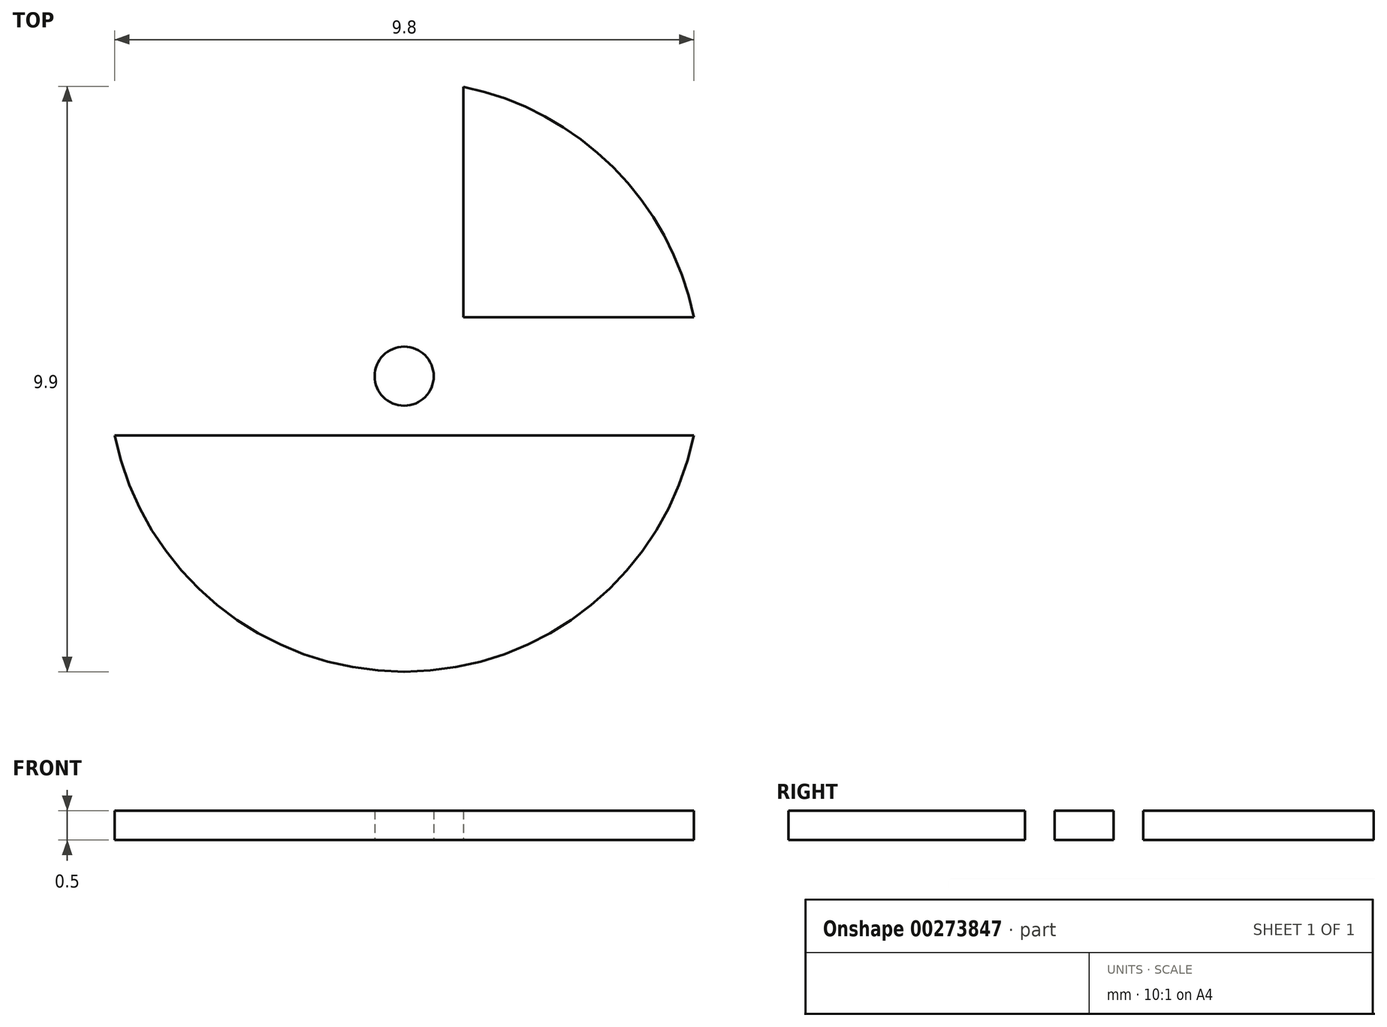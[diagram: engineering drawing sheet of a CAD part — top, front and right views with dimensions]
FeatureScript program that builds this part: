
annotation { "Feature Type Name" : "Feature", "Feature Type Description" : "" }
export const myFeature = defineFeature(function(context is Context, id is Id, definition is map)
    precondition{}
    {
        {
            var Q0;
            Q0=qCreatedBy(makeId("Top.planeOp"),FACE);
            var sketch = newSketch(context, id + "F0", { "sketchPlane" : qUnion([Q0])});
            skCircle(sketch, "E0", {"center": v(0, 0) * mm, "radius": 5 * mm});
            skLineSegment(sketch, "E1.bottom", {"start": v(-1, 12.5) * mm, "end": v(1, 12.5) * mm});
            skLineSegment(sketch, "E1.top", {"start": v(-1, -12.5) * mm, "end": v(1, -12.5) * mm});
            skLineSegment(sketch, "E1.left", {"start": v(-1, 12.5) * mm, "end": v(-1, -12.5) * mm});
            skLineSegment(sketch, "E1.right", {"start": v(1, 12.5) * mm, "end": v(1, -12.5) * mm});
            skLineSegment(sketch, "E2.bottom", {"start": v(-12.5, 1) * mm, "end": v(12.5, 1) * mm});
            skLineSegment(sketch, "E2.top", {"start": v(-12.5, -1) * mm, "end": v(12.5, -1) * mm});
            skLineSegment(sketch, "E2.left", {"start": v(-12.5, 1) * mm, "end": v(-12.5, -1) * mm});
            skLineSegment(sketch, "E2.right", {"start": v(12.5, 1) * mm, "end": v(12.5, -1) * mm});
            skCircle(sketch, "E3", {"center": v(0, 0) * mm, "radius": 1 * mm});
            skCircle(sketch, "E4", {"center": v(0, 0) * mm, "radius": 0.5 * mm});
            skSolve(sketch);
        }
        {
            var Q0;
            Q0=makeQuery(id+"F0.imprint","IMPRINT",FACE,{"disambiguationData":[TD([[makeQuery(id+"F0.imprint","IMPRINT",EDGE,{"derivedFrom":sQuery(id+"F0.wireOp",EDGE,"E4")}),1.0]])]});
            var Q1;
            {var subQ0=sQuery(id+"F0.wireOp",EDGE,"E1.left");var subQ1=sQuery(id+"F0.wireOp",EDGE,"E0");var subQ2=makeQuery(id+"F0.imprint","INTERSECT",VERTEX,{"disambiguationData":[OD(0.0)],"derivedFrom":[subQ1,subQ0]});Q1=makeQuery(id+"F0.imprint","IMPRINT",FACE,{"disambiguationData":[TD([[makeQuery(id+"F0.imprint","IMPRINT",EDGE,{"disambiguationData":[TD([[subQ2,-1.0]])],"derivedFrom":subQ1}),1.0]])]});}
            var Q2;
            {var subQ0=sQuery(id+"F0.wireOp",EDGE,"E1.right");var subQ1=sQuery(id+"F0.wireOp",EDGE,"E0");var subQ2=makeQuery(id+"F0.imprint","INTERSECT",VERTEX,{"disambiguationData":[OD(0.0)],"derivedFrom":[subQ1,subQ0]});Q2=makeQuery(id+"F0.imprint","IMPRINT",FACE,{"disambiguationData":[TD([[makeQuery(id+"F0.imprint","IMPRINT",EDGE,{"disambiguationData":[TD([[subQ2,1.0]])],"derivedFrom":subQ1}),1.0]])]});}
            var Q3;
            {var subQ0=sQuery(id+"F0.wireOp",EDGE,"E1.right");var subQ1=sQuery(id+"F0.wireOp",EDGE,"E0");var subQ2=makeQuery(id+"F0.imprint","INTERSECT",VERTEX,{"disambiguationData":[OD(1.0)],"derivedFrom":[subQ1,subQ0]});Q3=makeQuery(id+"F0.imprint","IMPRINT",FACE,{"disambiguationData":[TD([[makeQuery(id+"F0.imprint","IMPRINT",EDGE,{"disambiguationData":[TD([[subQ2,-1.0]])],"derivedFrom":subQ1}),1.0]])]});}
            var Q4;
            {var subQ0=sQuery(id+"F0.wireOp",EDGE,"E2.top");var subQ1=sQuery(id+"F0.wireOp",EDGE,"E0");var subQ2=makeQuery(id+"F0.imprint","INTERSECT",VERTEX,{"disambiguationData":[OD(0.0)],"derivedFrom":[subQ1,subQ0]});Q4=makeQuery(id+"F0.imprint","IMPRINT",FACE,{"disambiguationData":[TD([[makeQuery(id+"F0.imprint","IMPRINT",EDGE,{"disambiguationData":[TD([[subQ2,-1.0]])],"derivedFrom":subQ1}),1.0]])]});}
            extrude(context, id + "F1", {"entities" : qUnion([Q0, Q1, Q2, Q3, Q4]), "depth" : 0.5 * mm});
        }
    });
